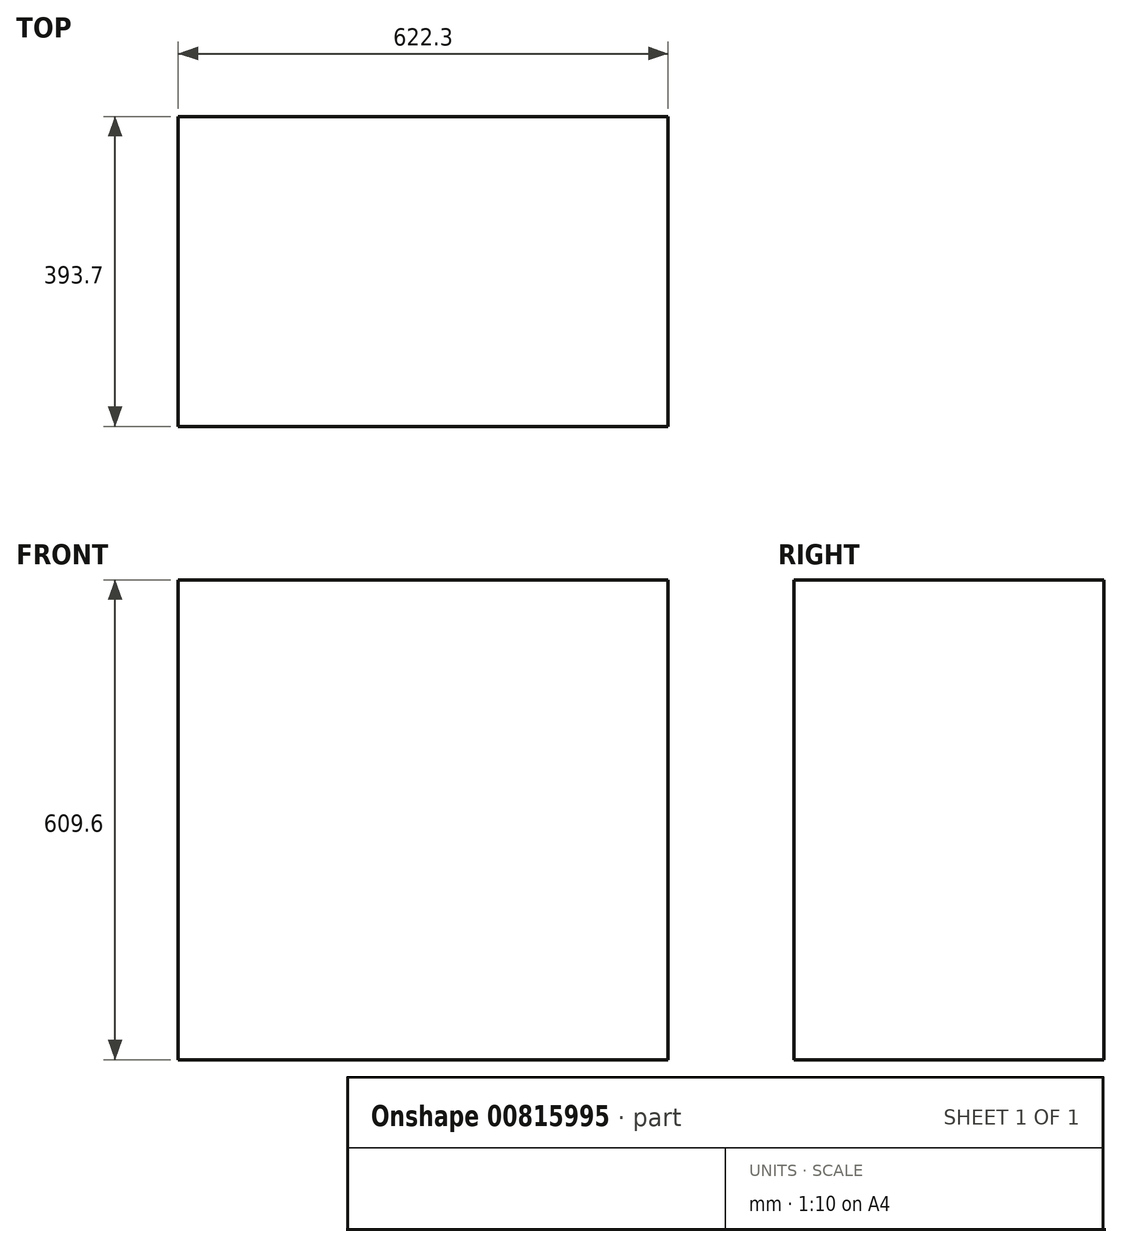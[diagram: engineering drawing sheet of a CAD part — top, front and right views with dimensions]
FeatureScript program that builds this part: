
annotation { "Feature Type Name" : "Feature", "Feature Type Description" : "" }
export const myFeature = defineFeature(function(context is Context, id is Id, definition is map)
    precondition{}
    {
        {
            var Q0;
            Q0=qCreatedBy(makeId("Top.planeOp"),FACE);
            var sketch = newSketch(context, id + "F0", { "sketchPlane" : qUnion([Q0])});
            skLineSegment(sketch, "E0.bottom", {"start": v(-311.15, 196.85) * mm, "end": v(311.15, 196.85) * mm});
            skLineSegment(sketch, "E0.top", {"start": v(-311.15, -196.85) * mm, "end": v(311.15, -196.85) * mm});
            skLineSegment(sketch, "E0.left", {"start": v(-311.15, 196.85) * mm, "end": v(-311.15, -196.85) * mm});
            skLineSegment(sketch, "E0.right", {"start": v(311.15, 196.85) * mm, "end": v(311.15, -196.85) * mm});
            skPoint(sketch, "E0.middle", {"position": v(0, 0) * mm});
            skSolve(sketch);
        }
        {
            var Q0;
            Q0 = qSketchRegion(id + "F0", true);
            extrude(context, id + "F1", {"entities" : qUnion([Q0]), "depth" : 609.6 * mm, "offsetDistance" : 25.4 * mm});
        }
    });
